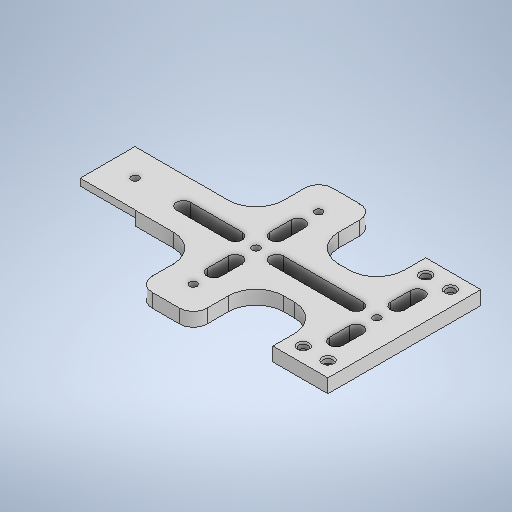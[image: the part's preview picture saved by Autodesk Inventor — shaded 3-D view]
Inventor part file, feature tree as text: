
AUTODESK INVENTOR PART (.ipt)
format: ipt  version: 2025.2 (Build 292293000, 293)  size: 452,096 bytes
history: native  units: mm
features: extrude x10, sketch x10, fillet x4
ambient origin geometry x8: Origin, YZ Plane, XZ Plane, XY Plane, X Axis, Y Axis, Z Axis, Center Point
bodies: Solid1 (feature_tree)
feature tree (24):
  extrude  "Extrusion1"  Depth=111.0mm
  extrude  "Extrusion2"  Depth=10.0mm
  fillet  "Fillet1"  Radius=40.0mm
  fillet  "Fillet2"  Radius=10.0mm
  sketch  "Sketch3"  dims[d7=6.5mm d8=6.5mm]
  extrude  "Extrusion3"  Depth=6.5mm
  extrude  "Extrusion4"  Depth=6.5mm
  extrude  "Extrusion5"  Depth=1.0mm
  extrude  "Extrusion6"  Depth=25.0mm
  extrude  "Extrusion7"  Depth=15.0mm
  extrude  "Extrusion8"  Depth=40.0mm TaperAngle=0.0deg
  extrude  "Extrusion9"  Depth=10.0mm
  fillet  "Fillet4"  Radius=15.0mm
  fillet  "Fillet5"  Radius=10.0mm
  extrude  "Extrusion10"  Depth=40.0mm TaperAngle=0.0deg
  sketch  "Sketch1"  dims[d0=40.0mm d1=111.0mm]
  sketch  "Sketch2"  dims[d2=3.6mm d3=5.5mm d4=40.0mm d5=10.0mm d6=0.0mm]
  sketch  "Sketch4"  dims[d11=4.0mm d12=0.0mm d13=1.0mm]
  sketch  "Sketch5"  dims[d14=20.0mm d15=25.0mm]
  sketch  "Sketch6"  dims[d16=5.0mm d17=15.0mm]
  sketch  "Sketch Rectangular Pattern3"  dims[d9=6.5mm d10=6.5mm]
  sketch  "Sketch8"  dims[d18=5.0mm d19=40.0mm d20=0.0mm]
  sketch  "Sketch9"  dims[d21=40.0mm d22=0.0mm d33=10.0mm d34=15.0mm d35=10.0mm d36=0.0mm]
  sketch  "Sketch11"  dims[d49=15.0mm d51=40.0mm d52=0.0mm d53=15.0mm d54=5.0mm d55=5.5mm d56=20.0mm d58=87.75mm d59=10.0mm d61=10.0mm d63=10.0mm d64=10.0mm d65=0.0mm d66=0.0mm d67=40.0mm d68=40.0mm d69=45.5mm d70=45.5mm d71=10.0mm d72=0.0mm d74=5.5mm d75=10.0mm d76=10.0mm d77=10.0mm d78=0.0mm d79=20.0mm d80=10.0mm d81=40.0mm d82=0.15mm d83=40.0mm d84=0.15mm d85=0.0mm d86=0.0mm]
